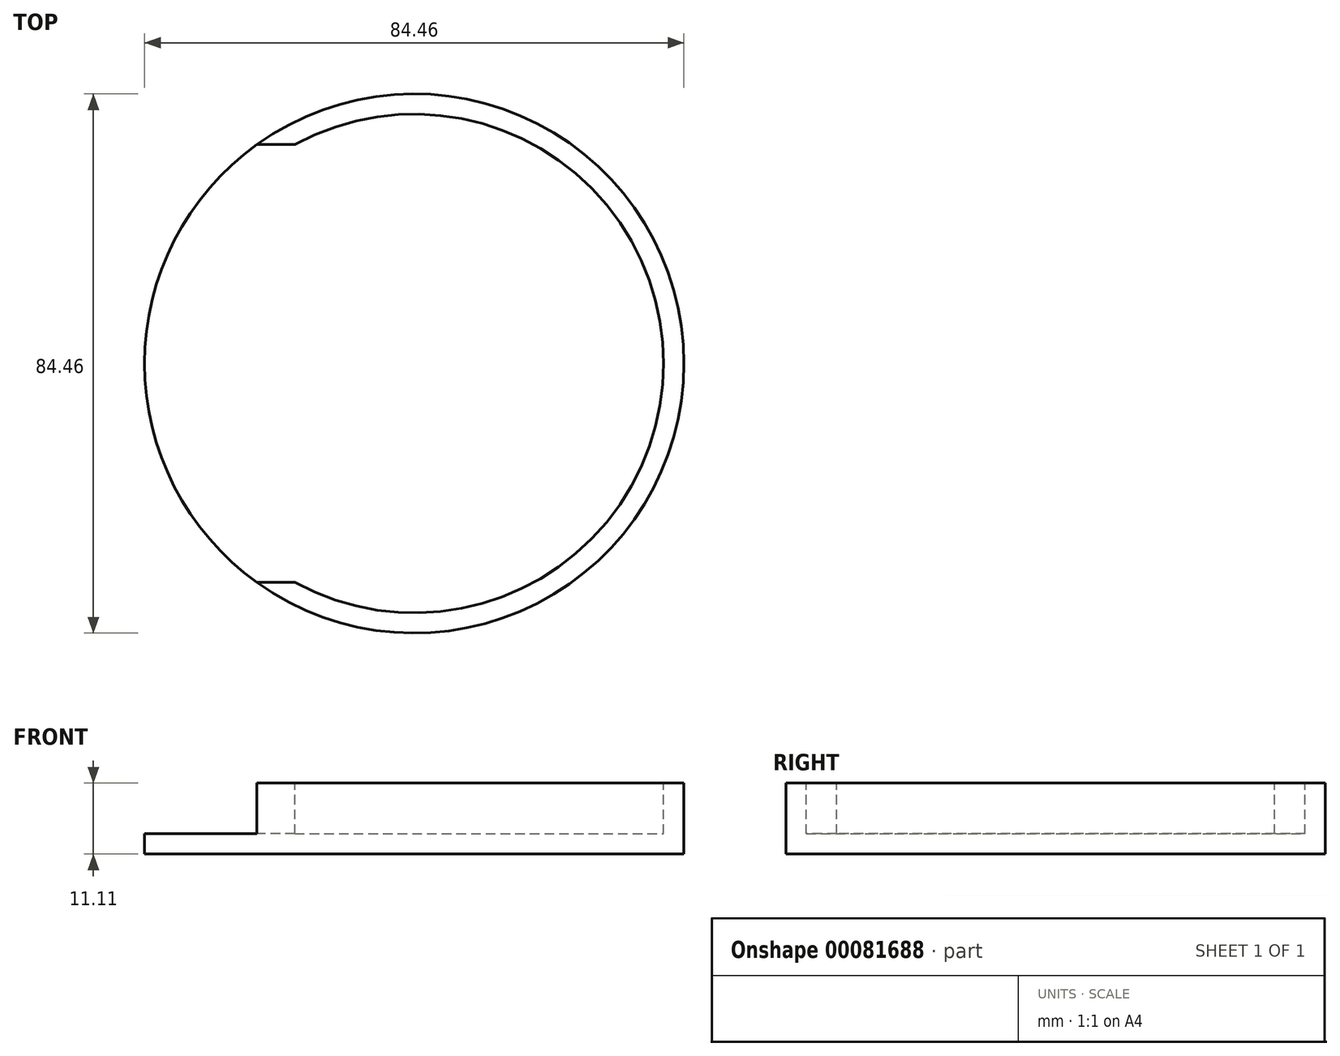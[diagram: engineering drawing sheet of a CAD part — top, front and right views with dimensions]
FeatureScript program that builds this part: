
annotation { "Feature Type Name" : "Feature", "Feature Type Description" : "" }
export const myFeature = defineFeature(function(context is Context, id is Id, definition is map)
    precondition{}
    {
        {
            var Q0;
            Q0=qCreatedBy(makeId("Top.planeOp"),FACE);
            var sketch = newSketch(context, id + "F2", { "sketchPlane" : qUnion([Q0])});
            skCircle(sketch, "E0", {"center": v(0, 0) * mm, "radius": 42.23 * mm});
            skSolve(sketch);
        }
        {
            var Q0;
            Q0=makeQuery(id+"F2.imprint","IMPRINT",FACE,{"disambiguationData":[TD([[makeQuery(id+"F2.imprint","IMPRINT",EDGE,{"derivedFrom":sQuery(id+"F2.wireOp",EDGE,"E0")}),1.0]])]});
            extrude(context, id + "F0", {"entities" : qUnion([Q0]), "oppositeDirection" : true, "depth" : 11.1 * mm});
        }
        {
            var Q0;
            Q0=makeQuery(id+"F0.opExtrude","CAP_FACE",FACE,{"disambiguationData":[OSD([sQuery(id+"F2.wireOp",EDGE,"E0")])],"isStart":true});
            shell(context, id + "F3", {"entities" : qUnion([Q0]), "thickness" : 3.17 * mm});
        }
        {
            var Q0;
            {var subQ0=sQuery(id+"F2.wireOp",EDGE,"E0");Q0=makeQuery(id+"F3.opShell","OFFSET_FACE",FACE,{"disambiguationData":[OSD([subQ0]),TDD([makeQuery(id+"F0.opExtrude","CAP_FACE",FACE,{"disambiguationData":[OSD([subQ0])],"isStart":false})])]});}
            var sketch = newSketch(context, id + "F1", { "sketchPlane" : qUnion([Q0])});
            skCircle(sketch, "E1", {"center": v(0, 0) * mm, "radius": 34.8 * mm});
            skCircle(sketch, "E2", {"center": v(0, 0) * mm, "radius": 34.3 * mm});
            skLineSegment(sketch, "E3", {"start": v(0, 34.3) * mm, "end": v(-44.45, 34.3) * mm});
            skLineSegment(sketch, "E4", {"start": v(0, -34.3) * mm, "end": v(-44.45, -34.3) * mm});
            skLineSegment(sketch, "E5", {"start": v(-44.45, -34.3) * mm, "end": v(-44.45, 34.3) * mm});
            skSolve(sketch);
        }
        {
            var Q0;
            {var subQ0=sQuery(id+"F1.wireOp",EDGE,"E5");Q0=makeQuery(id+"F1.imprint","IMPRINT",FACE,{"disambiguationData":[TD([[makeQuery(id+"F1.imprint","IMPRINT",EDGE,{"derivedFrom":subQ0}),-1.0]])]});}
            var Q1;
            Q1=makeQuery(id+"F0.opExtrude","CAP_FACE",FACE,{"disambiguationData":[OSD([sQuery(id+"F2.wireOp",EDGE,"E0")])],"isStart":true});
            var Q2;
            {var subQ0=sQuery(id+"F1.wireOp",EDGE,"E3");var subQ1=sQuery(id+"F1.wireOp",EDGE,"E1");var subQ2=makeQuery(id+"F1.imprint","INTERSECT",VERTEX,{"derivedFrom":[subQ1,subQ0]});Q2=makeQuery(id+"F1.imprint","IMPRINT",FACE,{"disambiguationData":[TD([[makeQuery(id+"F1.imprint","IMPRINT",EDGE,{"disambiguationData":[TD([[subQ2,-1.0]])],"derivedFrom":subQ1}),-1.0]])]});}
            var Q3;
            {var subQ0=sQuery(id+"F1.wireOp",EDGE,"E3");var subQ1=sQuery(id+"F1.wireOp",EDGE,"E1");var subQ2=makeQuery(id+"F1.imprint","INTERSECT",VERTEX,{"derivedFrom":[subQ1,subQ0]});Q3=makeQuery(id+"F1.imprint","IMPRINT",FACE,{"disambiguationData":[TD([[makeQuery(id+"F1.imprint","IMPRINT",EDGE,{"disambiguationData":[TD([[subQ2,-1.0]])],"derivedFrom":subQ1}),1.0]])]});}
            extrude(context, id + "F4", {"entities" : qUnion([Q0, Q1, Q2, Q3]), "operationType" : NewBodyOperationType.REMOVE, "depth" : 25.4 * mm});
        }
    });
